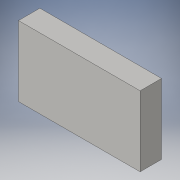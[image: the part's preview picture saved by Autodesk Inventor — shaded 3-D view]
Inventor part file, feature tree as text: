
AUTODESK INVENTOR PART (.ipt)
format: ipt  version: 2016 (Build 200138000, 138)  size: 82,432 bytes
history: native  units: in
note: dims shown in document units (in); Inventor stores cm internally (conversion verified against a paired STEP export)
features: extrude x1, sketch x1
ambient origin geometry x8: Origin, YZ Plane, XZ Plane, XY Plane, X Axis, Y Axis, Z Axis, Center Point
bodies: Solid1 (feature_tree)
feature tree (2):
  extrude  "Extrusion1"  Depth=29.5276in
  sketch  "Sketch1"  dims[d0=51.1811in d1=29.5276in d2=9.0in d3=0.0in]
